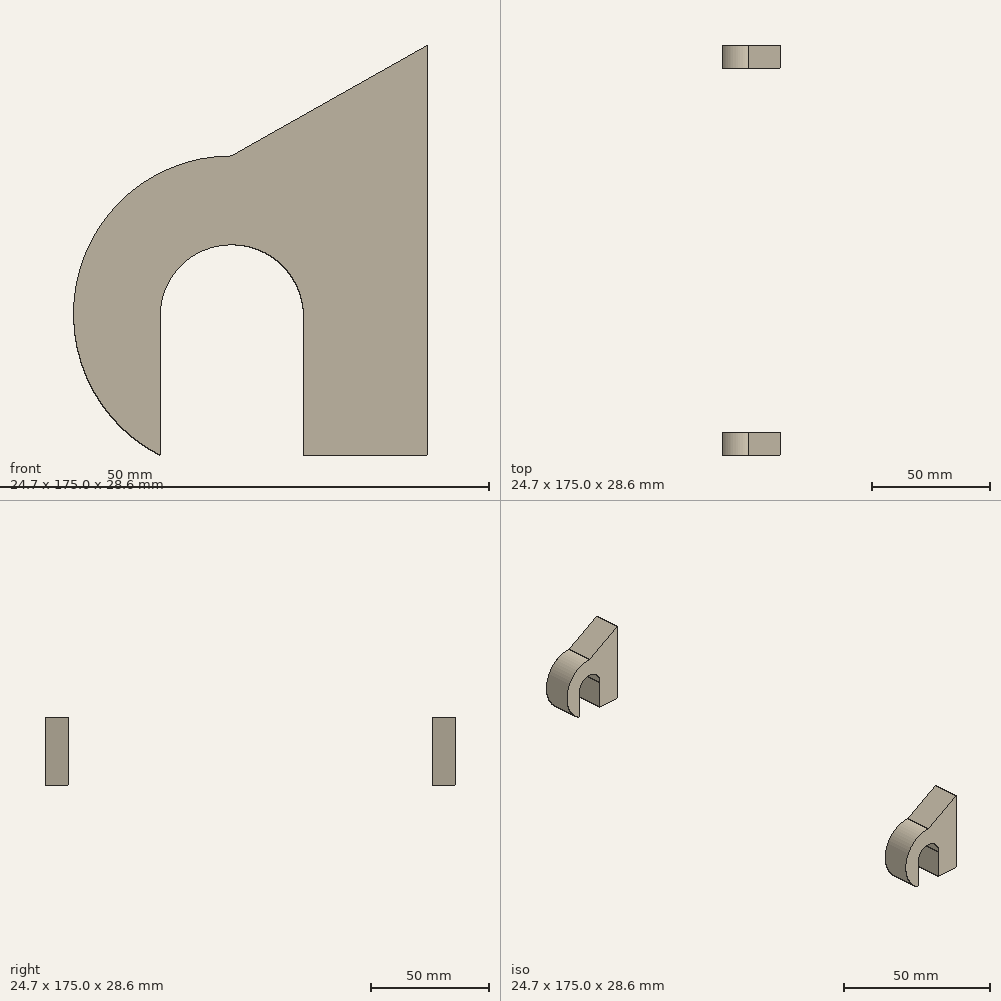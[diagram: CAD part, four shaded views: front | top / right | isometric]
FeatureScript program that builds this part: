
annotation { "Feature Type Name" : "Feature", "Feature Type Description" : "" }
export const myFeature = defineFeature(function(context is Context, id is Id, definition is map)
    precondition{}
    {
        {
            var Q0;
            Q0=qCreatedBy(makeId("Front.planeOp"),FACE);
            var sketch = newSketch(context, id + "F0", { "sketchPlane" : qUnion([Q0])});
            skLineSegment(sketch, "E0", {"start": v(5, 0) * mm, "end": v(5, -9.7) * mm});
            skLineSegment(sketch, "E1", {"start": v(-5, 0) * mm, "end": v(-5, -9.7) * mm});
            skArc(sketch, "E2", {"start": v(5, -9.7) * mm, "mid": v(0, 11.2) * mm, "end": v(-5, -9.7) * mm});
            skArc(sketch, "E3", {"start": v(5, 0) * mm, "mid": v(0, 5) * mm, "end": v(-5, 0) * mm});
            skLineSegment(sketch, "E4", {"start": v(0, 11.2) * mm, "end": v(13.66, 18.91) * mm});
            skLineSegment(sketch, "E5", {"start": v(5, -9.7) * mm, "end": v(13.66, -9.7) * mm});
            skLineSegment(sketch, "E6", {"start": v(13.66, -9.7) * mm, "end": v(13.66, 18.91) * mm});
            skSolve(sketch);
        }
        {
            var Q0;
            Q0 = qSketchRegion(id + "F0", true);
            extrude(context, id + "F1", {"entities" : qUnion([Q0]), "depth" : 10 * mm});
        }
        {
            var Q0;
            Q0=makeQuery(id+"F1.opExtrude","CAP_FACE",FACE,{"disambiguationData":[OSD([sQuery(id+"F0.wireOp",EDGE,"E0"),sQuery(id+"F0.wireOp",EDGE,"E1"),sQuery(id+"F0.wireOp",EDGE,"E2"),sQuery(id+"F0.wireOp",EDGE,"E3"),sQuery(id+"F0.wireOp",EDGE,"E4"),sQuery(id+"F0.wireOp",EDGE,"E5"),sQuery(id+"F0.wireOp",EDGE,"E6")])],"isStart":true});
            var sketch = newSketch(context, id + "F2", { "sketchPlane" : qUnion([Q0])});
            skSolve(sketch);
        }
        {
            var Q0;
            Q0 = qSketchRegion(id + "F2", true);
            var Q1;
            Q1=makeQuery(id+"F2.imprint","IMPRINT",FACE,{"disambiguationData":[TD([[makeQuery(id+"F2.imprint","IMPRINT",EDGE,{"derivedFrom":makeQuery(id+"F1.opExtrude","CAP_EDGE",EDGE,{"disambiguationData":[OSD([sQuery(id+"F0.wireOp",EDGE,"E0")])],"isStart":true})}),-1.0]])]});
            extrude(context, id + "F3", {"entities" : qUnion([Q0, Q1]), "depth" : 155 * mm});
        }
        {
            var Q0;
            Q0=makeQuery(id+"F3.opExtrude","CAP_FACE",FACE,{"disambiguationData":[OSD([sQuery(id+"F0.wireOp",EDGE,"E0"),sQuery(id+"F0.wireOp",EDGE,"E1"),sQuery(id+"F0.wireOp",EDGE,"E2"),sQuery(id+"F0.wireOp",EDGE,"E3"),sQuery(id+"F0.wireOp",EDGE,"E4"),sQuery(id+"F0.wireOp",EDGE,"E5"),sQuery(id+"F0.wireOp",EDGE,"E6")])],"isStart":false});
            var sketch = newSketch(context, id + "F4", { "sketchPlane" : qUnion([Q0])});
            skSolve(sketch);
        }
        {
            var Q0;
            Q0 = qSketchRegion(id + "F4", true);
            var Q1;
            Q1=makeQuery(id+"F4.imprint","IMPRINT",FACE,{"disambiguationData":[TD([[makeQuery(id+"F4.imprint","IMPRINT",EDGE,{"derivedFrom":makeQuery(id+"F3.opExtrude","CAP_EDGE",EDGE,{"disambiguationData":[OSD([sQuery(id+"F0.wireOp",EDGE,"E0")])],"isStart":false})}),-1.0]])]});
            extrude(context, id + "F5", {"entities" : qUnion([Q0, Q1]), "depth" : 10 * mm});
        }
        {
            var Q0;
            Q0=makeQuery(id+"F3.opExtrude","SWEPT_BODY",BODY,{"disambiguationData":[OSD([sQuery(id+"F0.wireOp",EDGE,"E0"),sQuery(id+"F0.wireOp",EDGE,"E1"),sQuery(id+"F0.wireOp",EDGE,"E2"),sQuery(id+"F0.wireOp",EDGE,"E3"),sQuery(id+"F0.wireOp",EDGE,"E4"),sQuery(id+"F0.wireOp",EDGE,"E5"),sQuery(id+"F0.wireOp",EDGE,"E6")])]});
            deleteBodies(context, id + "F6", {"entities" : qUnion([Q0])});
        }
    });
